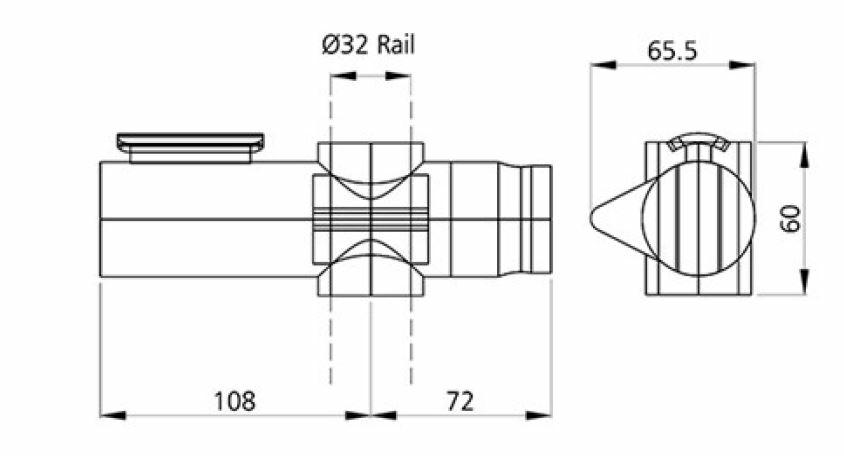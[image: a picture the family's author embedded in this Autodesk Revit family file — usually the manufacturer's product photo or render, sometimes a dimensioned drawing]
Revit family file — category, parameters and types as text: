
# Revit family: rba-bim-rba4110-936
name_source: partatom
category: Plumbing Fixtures
revit_build: Autodesk Revit 2018 (Build: 20170223_1515(x64)
units: mm (PartAtom-declared; Revit-internal decimal feet)

## family parameters
Always vertical = Yes
Cut with Voids When Loaded = No
Part Type = Normal
Room Calculation Point = No
Round Connector Dimension = Use Diameter
Shared = Yes
Work Plane-Based = No

## types (1)
- RBA4110-936
    CW Connection = Yes
    Description = RH T-Rail for Showers, incl Slider & 4 Star Handset
    Distance Away from Toilet (default) = 1090 mm  [stored 3.57612 ft]
    Distance Away from Wall (default) = 100 mm  [stored 0.328084 ft]
    HW Connection = Yes
    Manufacturer = RBA Group
    Materials and Finishes = Chrome w/ Stainless Steel Hose
    Model = RBA4110-936
    Modified Issue = 20201019.01
    OFFSET = 1000 mm  [stored 3.28084 ft]
    URL = www.rba.com.au
    Vent Connection = Yes
    Waste Connection = Yes

note: [stored X ft] marks values corroborated as IEEE doubles in the binary element streams (Revit-internal decimal feet)

## geometry (parser evidence)
native form markers: Blend x12, Sweep x21
no freeform markers — native parametric forms only
